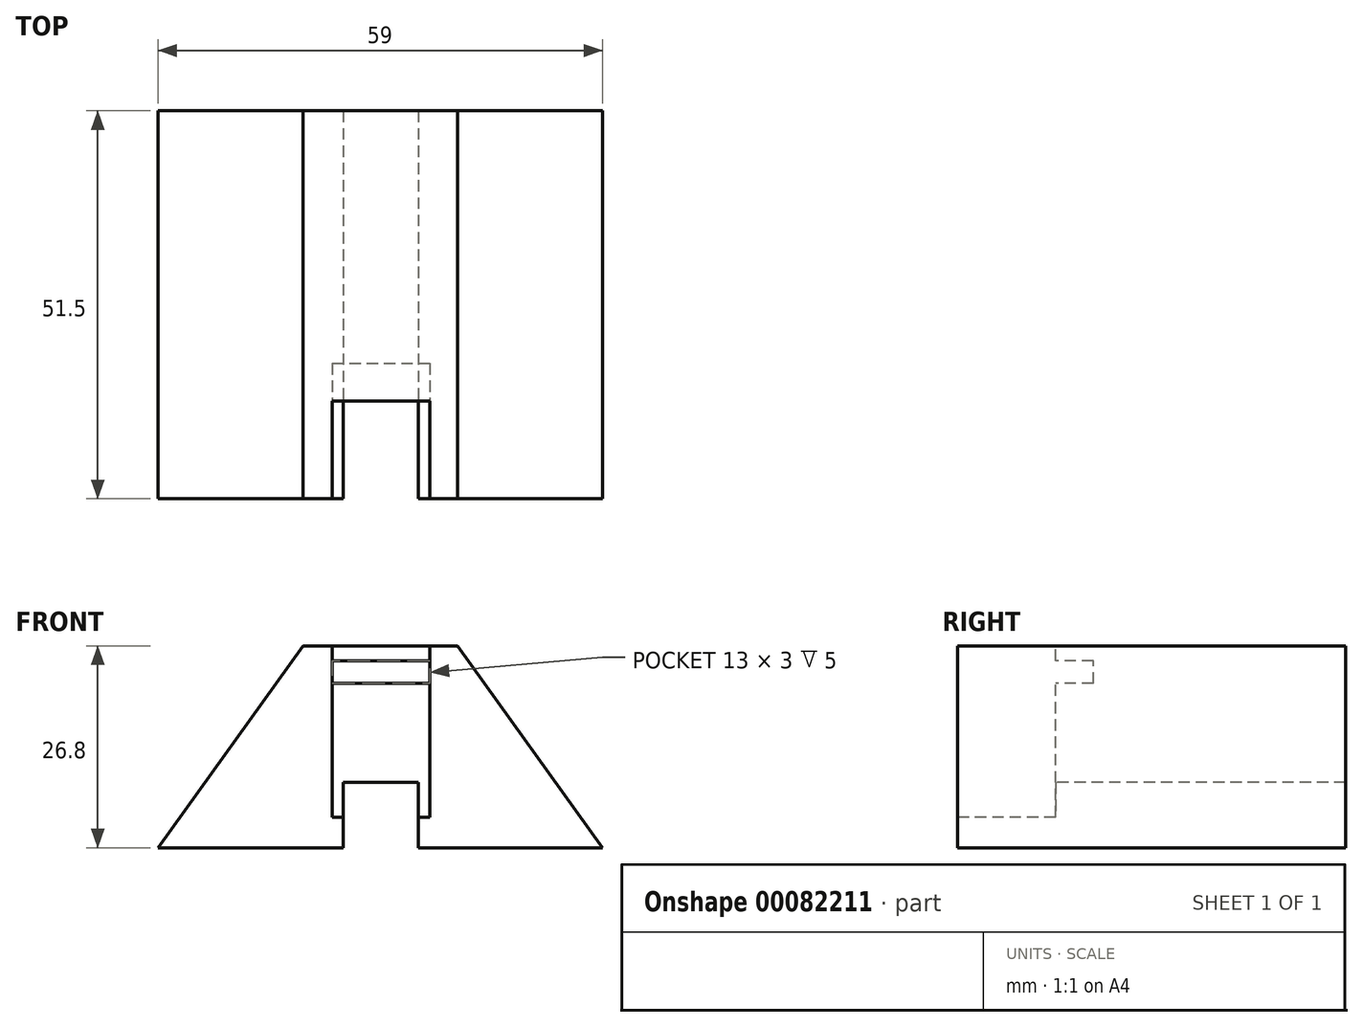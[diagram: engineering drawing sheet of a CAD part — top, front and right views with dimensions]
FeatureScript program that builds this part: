
annotation { "Feature Type Name" : "Feature", "Feature Type Description" : "" }
export const myFeature = defineFeature(function(context is Context, id is Id, definition is map)
    precondition{}
    {
        {
            var Q0;
            Q0=qCreatedBy(makeId("Top.planeOp"),FACE);
            var sketch = newSketch(context, id + "F0", { "sketchPlane" : qUnion([Q0])});
            skLineSegment(sketch, "E0.bottom", {"start": v(-29.5, -25.75) * mm, "end": v(29.5, -25.75) * mm});
            skLineSegment(sketch, "E0.top", {"start": v(-29.5, 25.75) * mm, "end": v(29.5, 25.75) * mm});
            skLineSegment(sketch, "E0.left", {"start": v(-29.5, -25.75) * mm, "end": v(-29.5, 25.75) * mm});
            skLineSegment(sketch, "E0.right", {"start": v(29.5, -25.75) * mm, "end": v(29.5, 25.75) * mm});
            skPoint(sketch, "E0.middle", {"position": v(0, 0) * mm});
            skLineSegment(sketch, "E1", {"start": v(0, 25.75) * mm, "end": v(0, -25.75) * mm, "construction": true});
            skSolve(sketch);
        }
        {
            var Q0;
            Q0=makeQuery(id+"F0.imprint","IMPRINT",FACE,{"disambiguationData":[TD([[makeQuery(id+"F0.imprint","IMPRINT",EDGE,{"derivedFrom":sQuery(id+"F0.wireOp",EDGE,"E0.bottom")}),1.0]])]});
            extrude(context, id + "F1", {"entities" : qUnion([Q0]), "depth" : 26.8 * mm});
        }
        {
            var Q0;
            Q0=makeQuery(id+"F1.opExtrude","SWEPT_FACE",FACE,{"disambiguationData":[OSD([sQuery(id+"F0.wireOp",EDGE,"E0.bottom")])]});
            var sketch = newSketch(context, id + "F2", { "sketchPlane" : qUnion([Q0])});
            skLineSegment(sketch, "E2", {"start": v(-29.5, 0) * mm, "end": v(-10.24, 26.8) * mm});
            skLineSegment(sketch, "E3", {"start": v(-10.24, 26.8) * mm, "end": v(-29.5, 26.8) * mm});
            skLineSegment(sketch, "E4", {"start": v(-29.5, 26.8) * mm, "end": v(-29.5, 0) * mm});
            skLineSegment(sketch, "E5", {"start": v(29.5, 0) * mm, "end": v(10.24, 26.8) * mm});
            skLineSegment(sketch, "E6", {"start": v(10.24, 26.8) * mm, "end": v(29.5, 26.8) * mm});
            skLineSegment(sketch, "E7", {"start": v(29.5, 26.8) * mm, "end": v(29.5, 0) * mm});
            skSolve(sketch);
        }
        {
            var Q0;
            Q0=makeQuery(id+"F2.imprint","IMPRINT",FACE,{"disambiguationData":[TD([[makeQuery(id+"F2.imprint","IMPRINT",EDGE,{"derivedFrom":sQuery(id+"F2.wireOp",EDGE,"E5")}),-1.0]])]});
            var Q1;
            Q1=makeQuery(id+"F2.imprint","IMPRINT",FACE,{"disambiguationData":[TD([[makeQuery(id+"F2.imprint","IMPRINT",EDGE,{"derivedFrom":sQuery(id+"F2.wireOp",EDGE,"E2")}),1.0]])]});
            extrude(context, id + "F3", {"entities" : qUnion([Q0, Q1]), "operationType" : NewBodyOperationType.REMOVE, "endBound" : BoundingType.THROUGH_ALL, "oppositeDirection" : true, "depth" : 25.4 * mm});
        }
        {
            var Q0;
            Q0=makeQuery(id+"F1.opExtrude","CAP_FACE",FACE,{"disambiguationData":[OSD([sQuery(id+"F0.wireOp",EDGE,"E0.bottom"),sQuery(id+"F0.wireOp",EDGE,"E0.top"),sQuery(id+"F0.wireOp",EDGE,"E0.left"),sQuery(id+"F0.wireOp",EDGE,"E0.right")])],"isStart":false});
            var sketch = newSketch(context, id + "F4", { "sketchPlane" : qUnion([Q0])});
            skLineSegment(sketch, "E8.bottom", {"start": v(-6.4, -12.75) * mm, "end": v(6.6, -12.75) * mm});
            skLineSegment(sketch, "E8.top", {"start": v(-6.4, -25.75) * mm, "end": v(6.6, -25.75) * mm});
            skLineSegment(sketch, "E8.left", {"start": v(-6.4, -12.75) * mm, "end": v(-6.4, -25.75) * mm});
            skLineSegment(sketch, "E8.right", {"start": v(6.6, -12.75) * mm, "end": v(6.6, -25.75) * mm});
            skSolve(sketch);
        }
        {
            var Q0;
            Q0=qSketchRegion(id+"F4",true);
            extrude(context, id + "F5", {"entities" : qUnion([Q0]), "operationType" : NewBodyOperationType.REMOVE, "oppositeDirection" : true, "depth" : 22.75 * mm});
        }
        {
            var Q0;
            Q0=makeQuery(id+"F5.boolean.opBoolean","COPY",FACE,{"derivedFrom":makeQuery(id+"F5.opExtrude","SWEPT_FACE",FACE,{"disambiguationData":[OSD([sQuery(id+"F4.wireOp",EDGE,"E8.bottom")])]})});
            var sketch = newSketch(context, id + "F6", { "sketchPlane" : qUnion([Q0])});
            skLineSegment(sketch, "E9.bottom", {"start": v(-6.4, 24.8) * mm, "end": v(6.6, 24.8) * mm});
            skLineSegment(sketch, "E9.top", {"start": v(-6.4, 21.8) * mm, "end": v(6.6, 21.8) * mm});
            skLineSegment(sketch, "E9.left", {"start": v(-6.4, 24.8) * mm, "end": v(-6.4, 21.8) * mm});
            skLineSegment(sketch, "E9.right", {"start": v(6.6, 24.8) * mm, "end": v(6.6, 21.8) * mm});
            skSolve(sketch);
        }
        {
            var Q0;
            Q0=qSketchRegion(id+"F6",true);
            extrude(context, id + "F7", {"entities" : qUnion([Q0]), "operationType" : NewBodyOperationType.REMOVE, "oppositeDirection" : true, "depth" : 5 * mm});
        }
        {
            var Q0;
            Q0=makeQuery(id+"F1.opExtrude","SWEPT_FACE",FACE,{"disambiguationData":[OSD([sQuery(id+"F0.wireOp",EDGE,"E0.bottom")])]});
            var sketch = newSketch(context, id + "F8", { "sketchPlane" : qUnion([Q0])});
            skLineSegment(sketch, "E10", {"start": v(0, 26.8) * mm, "end": v(0, -4) * mm, "construction": true});
            skSolve(sketch);
        }
        {
            var Q0;
            {var subQ2=sQuery(id+"F0.wireOp",EDGE,"E0.bottom");Q0=makeQuery(id+"F8.imprint","IMPRINT",FACE,{"disambiguationData":[TD([[makeQuery(id+"F8.imprint","IMPRINT",EDGE,{"derivedFrom":makeQuery(id+"F1.opExtrude","CAP_EDGE",EDGE,{"disambiguationData":[OSD([subQ2])],"isStart":true})}),1.0]])]});}
            var sketch = newSketch(context, id + "F9", { "sketchPlane" : qUnion([Q0])});
            skLineSegment(sketch, "E11.bottom", {"start": v(-4.92, 8.67) * mm, "end": v(5.08, 8.67) * mm});
            skLineSegment(sketch, "E11.top", {"start": v(-4.92, 0) * mm, "end": v(5.08, 0) * mm});
            skLineSegment(sketch, "E11.left", {"start": v(-4.92, 8.67) * mm, "end": v(-4.92, 0) * mm});
            skLineSegment(sketch, "E11.right", {"start": v(5.08, 8.67) * mm, "end": v(5.08, 0) * mm});
            skSolve(sketch);
        }
        {
            var Q0;
            Q0=qSketchRegion(id+"F9",true);
            extrude(context, id + "F10", {"entities" : qUnion([Q0]), "operationType" : NewBodyOperationType.REMOVE, "endBound" : BoundingType.THROUGH_ALL, "oppositeDirection" : true, "depth" : 25.4 * mm});
        }
    });
